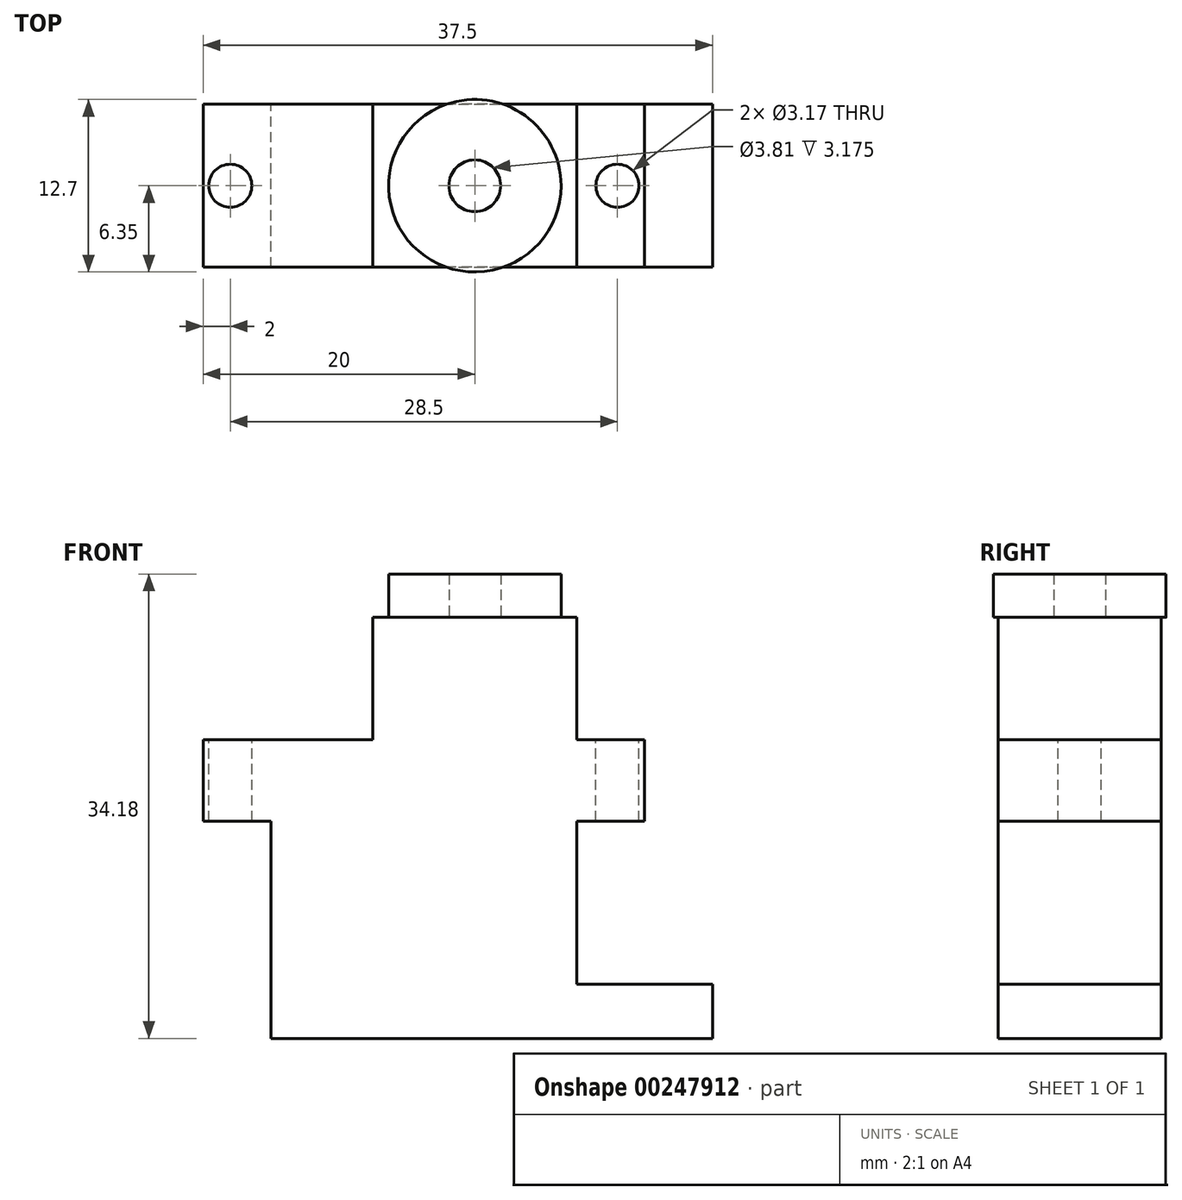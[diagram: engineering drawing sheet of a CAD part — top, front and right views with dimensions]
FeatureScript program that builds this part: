
annotation { "Feature Type Name" : "Feature", "Feature Type Description" : "" }
export const myFeature = defineFeature(function(context is Context, id is Id, definition is map)
    precondition{}
    {
        {
            var Q0;
            Q0=qCreatedBy(makeId("Front.planeOp"),FACE);
            var sketch = newSketch(context, id + "F0", { "sketchPlane" : qUnion([Q0])});
            skLineSegment(sketch, "E0.bottom", {"start": v(0, 0) * mm, "end": v(22.5, 0) * mm});
            skLineSegment(sketch, "E0.top", {"start": v(0, 16) * mm, "end": v(22.5, 16) * mm});
            skLineSegment(sketch, "E0.left", {"start": v(0, 0) * mm, "end": v(0, 16) * mm});
            skLineSegment(sketch, "E0.right", {"start": v(22.5, 0) * mm, "end": v(22.5, 16) * mm});
            skLineSegment(sketch, "E1.bottom", {"start": v(22.5, 0) * mm, "end": v(32.5, 0) * mm});
            skLineSegment(sketch, "E1.top", {"start": v(22.5, 4) * mm, "end": v(32.5, 4) * mm});
            skLineSegment(sketch, "E1.left", {"start": v(22.5, 0) * mm, "end": v(22.5, 4) * mm});
            skLineSegment(sketch, "E1.right", {"start": v(32.5, 0) * mm, "end": v(32.5, 4) * mm});
            skLineSegment(sketch, "E2.bottom", {"start": v(-5, 16) * mm, "end": v(27.5, 16) * mm});
            skLineSegment(sketch, "E2.top", {"start": v(-5, 22) * mm, "end": v(27.5, 22) * mm});
            skLineSegment(sketch, "E2.left", {"start": v(-5, 16) * mm, "end": v(-5, 22) * mm});
            skLineSegment(sketch, "E2.right", {"start": v(27.5, 16) * mm, "end": v(27.5, 22) * mm});
            skLineSegment(sketch, "E3.bottom", {"start": v(22.5, 22) * mm, "end": v(7.5, 22) * mm});
            skLineSegment(sketch, "E3.top", {"start": v(22.5, 31) * mm, "end": v(7.5, 31) * mm});
            skLineSegment(sketch, "E3.left", {"start": v(22.5, 22) * mm, "end": v(22.5, 31) * mm});
            skLineSegment(sketch, "E3.right", {"start": v(7.5, 22) * mm, "end": v(7.5, 31) * mm});
            skSolve(sketch);
        }
        {
            var Q0;
            Q0 = qSketchRegion(id + "F0", true);
            extrude(context, id + "F1", {"entities" : qUnion([Q0]), "depth" : 12 * mm});
        }
        {
            var Q0;
            {var subQ0=sQuery(id+"F0.wireOp",EDGE,"E2.top");Q0=makeQuery(id+"F1.opExtrude","SWEPT_FACE",FACE,{"disambiguationData":[OSD([subQ0]),TDD([makeQuery(id+"F0.imprint","IMPRINT",EDGE,{"disambiguationData":[TD([[makeQuery(id+"F0.imprint","INTERSECT",VERTEX,{"derivedFrom":[subQ0,sQuery(id+"F0.wireOp",EDGE,"E2.left")]}),-1.0]])],"derivedFrom":subQ0})])]});}
            var sketch = newSketch(context, id + "F2", { "sketchPlane" : qUnion([Q0])});
            skCircle(sketch, "E4", {"center": v(-3, -6) * mm, "radius": 1.59 * mm});
            skPoint(sketch, "E4.centerSnap0", {"position": v(-5, -6) * mm});
            skCircle(sketch, "E5", {"center": v(25.5, -6) * mm, "radius": 1.59 * mm});
            skSolve(sketch);
        }
        {
            var Q0;
            Q0 = qSketchRegion(id + "F2", true);
            extrude(context, id + "F3", {"entities" : qUnion([Q0]), "operationType" : NewBodyOperationType.REMOVE, "oppositeDirection" : true, "depth" : 10 * mm});
        }
        {
            var Q0;
            Q0=makeQuery(id+"F1.opExtrude","SWEPT_FACE",FACE,{"disambiguationData":[OSD([sQuery(id+"F0.wireOp",EDGE,"E3.top")])]});
            var sketch = newSketch(context, id + "F4", { "sketchPlane" : qUnion([Q0])});
            skCircle(sketch, "E6", {"center": v(15, -6) * mm, "radius": 6.35 * mm});
            skPoint(sketch, "E6.centerSnap0", {"position": v(15, 0) * mm});
            skPoint(sketch, "E6.centerSnap1", {"position": v(7.5, -6) * mm});
            skCircle(sketch, "E7", {"center": v(15, -6) * mm, "radius": 1.9 * mm});
            skSolve(sketch);
        }
        {
            var Q0;
            Q0 = qSketchRegion(id + "F4", true);
            extrude(context, id + "F5", {"entities" : qUnion([Q0]), "operationType" : NewBodyOperationType.ADD, "depth" : 3.17 * mm});
        }
    });
